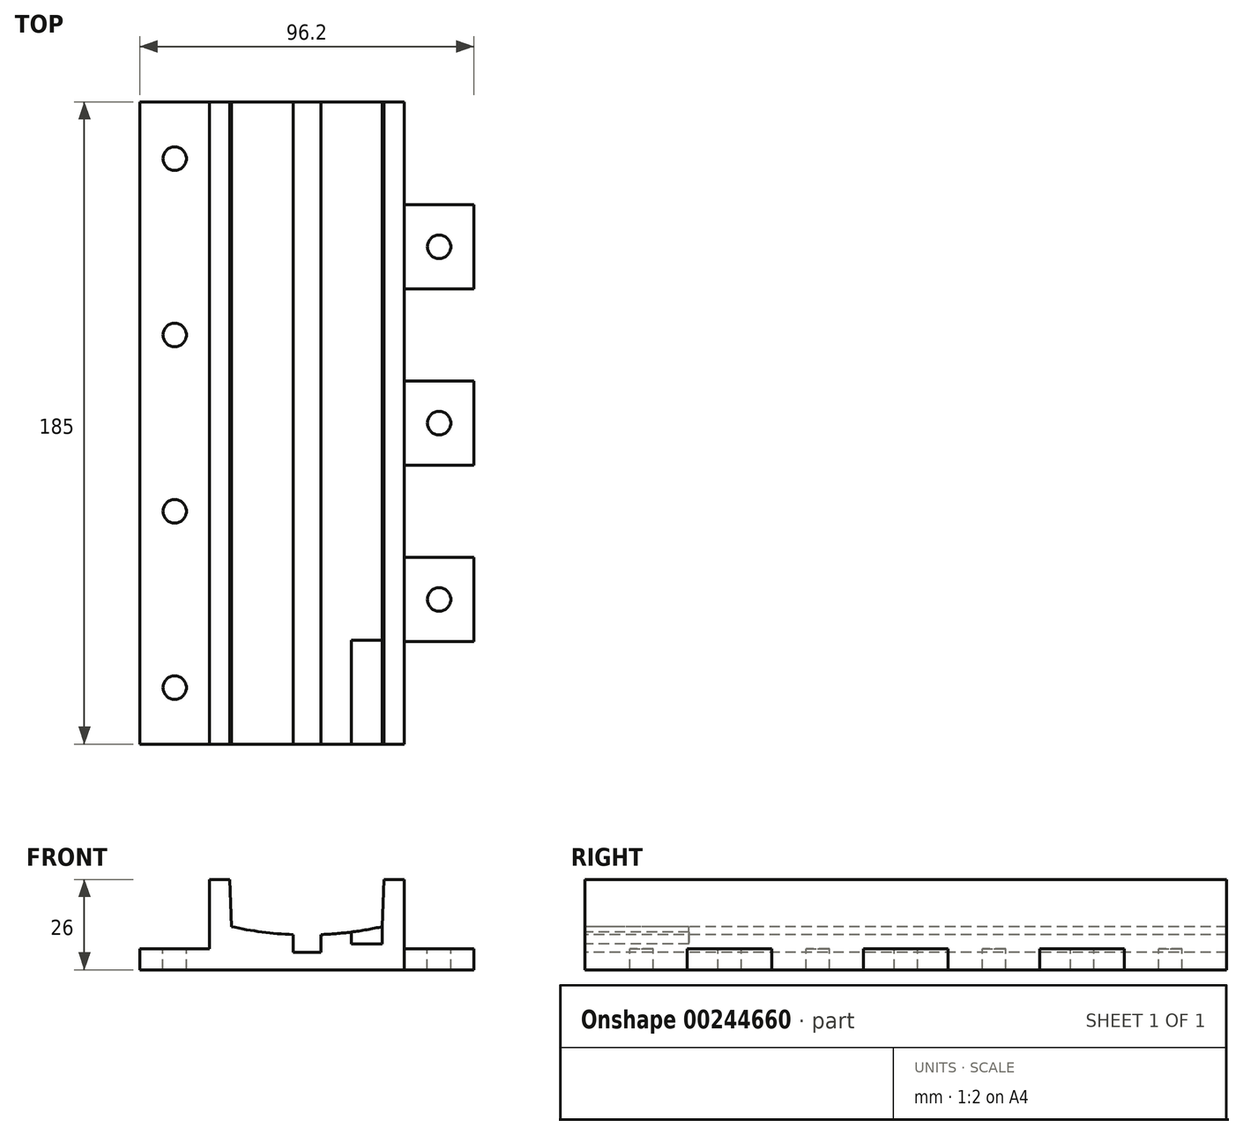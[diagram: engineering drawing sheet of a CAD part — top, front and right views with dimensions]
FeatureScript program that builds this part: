
annotation { "Feature Type Name" : "Feature", "Feature Type Description" : "" }
export const myFeature = defineFeature(function(context is Context, id is Id, definition is map)
    precondition{}
    {
        {
            var Q0;
            Q0=qCreatedBy(makeId("Front.planeOp"),FACE);
            var sketch = newSketch(context, id + "F0", { "sketchPlane" : qUnion([Q0])});
            skCircle(sketch, "E0", {"center": v(0, 0) * mm, "radius": 100.1 * mm});
            skLineSegment(sketch, "E1", {"start": v(0, 0) * mm, "end": v(0, -100.1) * mm});
            skLineSegment(sketch, "E2", {"start": v(0, -97.7) * mm, "end": v(21.77, -97.7) * mm});
            skLineSegment(sketch, "E3", {"start": v(0, -97.7) * mm, "end": v(-21.77, -97.7) * mm});
            skLineSegment(sketch, "E4", {"start": v(0, 0) * mm, "end": v(0, -27.77) * mm});
            skLineSegment(sketch, "E5", {"start": v(0, 0) * mm, "end": v(0, -84.15) * mm});
            skLineSegment(sketch, "E6", {"start": v(0, -84.15) * mm, "end": v(22.25, -84.15) * mm});
            skLineSegment(sketch, "E7", {"start": v(22.25, -84.15) * mm, "end": v(21.77, -97.7) * mm});
            skLineSegment(sketch, "E8", {"start": v(0, -84.15) * mm, "end": v(-22.25, -84.15) * mm});
            skLineSegment(sketch, "E9", {"start": v(-22.25, -84.15) * mm, "end": v(-21.77, -97.7) * mm});
            skLineSegment(sketch, "E10", {"start": v(-22.25, -84.15) * mm, "end": v(-28.1, -84.15) * mm});
            skLineSegment(sketch, "E11", {"start": v(-28.1, -84.15) * mm, "end": v(-28.1, -104.15) * mm});
            skLineSegment(sketch, "E12", {"start": v(-28.1, -104.15) * mm, "end": v(-48.1, -104.15) * mm});
            skLineSegment(sketch, "E13", {"start": v(-48.1, -104.15) * mm, "end": v(-48.1, -110.15) * mm});
            skLineSegment(sketch, "E14", {"start": v(-48.1, -110.15) * mm, "end": v(0, -110.15) * mm});
            skLineSegment(sketch, "E15", {"start": v(0, -110.15) * mm, "end": v(48.1, -110.15) * mm});
            skLineSegment(sketch, "E16", {"start": v(48.1, -110.15) * mm, "end": v(48.1, -104.15) * mm});
            skLineSegment(sketch, "E17", {"start": v(0, -97.7) * mm, "end": v(4, -97.7) * mm});
            skLineSegment(sketch, "E18", {"start": v(4, -105.15) * mm, "end": v(-4, -105.15) * mm});
            skLineSegment(sketch, "E19", {"start": v(-4, -105.15) * mm, "end": v(-4, -97.7) * mm});
            skLineSegment(sketch, "E20", {"start": v(4, -105.15) * mm, "end": v(4, -97.7) * mm});
            skLineSegment(sketch, "E21", {"start": v(21.77, -97.7) * mm, "end": v(12.77, -97.7) * mm});
            skLineSegment(sketch, "E22", {"start": v(12.77, -97.7) * mm, "end": v(12.77, -102.7) * mm});
            skLineSegment(sketch, "E23", {"start": v(12.77, -102.7) * mm, "end": v(21.77, -102.7) * mm});
            skLineSegment(sketch, "E24", {"start": v(21.77, -102.7) * mm, "end": v(21.77, -97.7) * mm});
            skLineSegment(sketch, "E25", {"start": v(22.25, -84.15) * mm, "end": v(28.1, -84.15) * mm});
            skLineSegment(sketch, "E26", {"start": v(28.1, -84.15) * mm, "end": v(28.1, -104.15) * mm});
            skLineSegment(sketch, "E27", {"start": v(28.1, -104.15) * mm, "end": v(48.1, -104.15) * mm});
            skSolve(sketch);
        }
        {
            var Q0;
            {var subQ0=sQuery(id+"F0.wireOp",EDGE,"E9");Q0=makeQuery(id+"F0.imprint","IMPRINT",FACE,{"disambiguationData":[TD([[makeQuery(id+"F0.imprint","IMPRINT",EDGE,{"derivedFrom":subQ0}),-1.0]])]});}
            var Q1;
            {var subQ4=sQuery(id+"F0.wireOp",EDGE,"E12");Q1=makeQuery(id+"F0.imprint","IMPRINT",FACE,{"disambiguationData":[TD([[makeQuery(id+"F0.imprint","IMPRINT",EDGE,{"derivedFrom":subQ4}),1.0]])]});}
            var Q2;
            {var subQ0=sQuery(id+"F0.wireOp",EDGE,"E7");Q2=makeQuery(id+"F0.imprint","IMPRINT",FACE,{"disambiguationData":[TD([[makeQuery(id+"F0.imprint","IMPRINT",EDGE,{"derivedFrom":subQ0}),1.0]])]});}
            var Q3;
            {var subQ0=sQuery(id+"F0.wireOp",EDGE,"E15");Q3=makeQuery(id+"F0.imprint","IMPRINT",FACE,{"disambiguationData":[TD([[makeQuery(id+"F0.imprint","IMPRINT",EDGE,{"derivedFrom":subQ0}),1.0]])]});}
            var Q4;
            {var subQ4=sQuery(id+"F0.wireOp",EDGE,"E23");Q4=makeQuery(id+"F0.imprint","IMPRINT",FACE,{"disambiguationData":[TD([[makeQuery(id+"F0.imprint","IMPRINT",EDGE,{"derivedFrom":subQ4}),1.0]])]});}
            extrude(context, id + "F1", {"entities" : qUnion([Q0, Q1, Q2, Q3, Q4]), "oppositeDirection" : true, "depth" : 185 * mm});
        }
        {
            var Q0;
            Q0=makeQuery(id+"F1.opExtrude","SWEPT_FACE",FACE,{"disambiguationData":[OSD([sQuery(id+"F0.wireOp",EDGE,"E12")])]});
            var sketch = newSketch(context, id + "F2", { "sketchPlane" : qUnion([Q0])});
            skLineSegment(sketch, "E28", {"start": v(-38.1, 0) * mm, "end": v(-38.1, 185) * mm});
            skLineSegment(sketch, "E29", {"start": v(-38.1, 0) * mm, "end": v(-38.1, 3.6) * mm});
            skLineSegment(sketch, "E30", {"start": v(-38.1, 3.6) * mm, "end": v(-38.1, 16.3) * mm});
            skLineSegment(sketch, "E31", {"start": v(-38.1, 16.3) * mm, "end": v(-38.1, 29) * mm});
            skLineSegment(sketch, "E32", {"start": v(-38.1, 29) * mm, "end": v(-38.1, 41.7) * mm});
            skLineSegment(sketch, "E33", {"start": v(-38.1, 41.7) * mm, "end": v(-38.1, 54.4) * mm});
            skLineSegment(sketch, "E34", {"start": v(-38.1, 54.4) * mm, "end": v(-38.1, 67.1) * mm});
            skLineSegment(sketch, "E35", {"start": v(-38.1, 67.1) * mm, "end": v(-38.1, 79.8) * mm});
            skLineSegment(sketch, "E36", {"start": v(-38.1, 79.8) * mm, "end": v(-38.1, 92.5) * mm});
            skLineSegment(sketch, "E37", {"start": v(-38.1, 92.5) * mm, "end": v(-38.1, 105.2) * mm});
            skLineSegment(sketch, "E38", {"start": v(-38.1, 105.2) * mm, "end": v(-38.1, 117.9) * mm});
            skLineSegment(sketch, "E39", {"start": v(-38.1, 117.9) * mm, "end": v(-38.1, 130.6) * mm});
            skLineSegment(sketch, "E40", {"start": v(-38.1, 130.6) * mm, "end": v(-38.1, 143.3) * mm});
            skLineSegment(sketch, "E41", {"start": v(-38.1, 143.3) * mm, "end": v(-38.1, 156) * mm});
            skLineSegment(sketch, "E42", {"start": v(-38.1, 156) * mm, "end": v(-38.1, 168.7) * mm});
            skLineSegment(sketch, "E43", {"start": v(-38.1, 168.7) * mm, "end": v(-38.1, 181.4) * mm});
            skLineSegment(sketch, "E44.bottom", {"start": v(-48.1, 3.6) * mm, "end": v(-28.1, 3.6) * mm});
            skLineSegment(sketch, "E44.top", {"start": v(-48.1, 29) * mm, "end": v(-28.1, 29) * mm});
            skLineSegment(sketch, "E44.left", {"start": v(-48.1, 3.6) * mm, "end": v(-48.1, 29) * mm});
            skLineSegment(sketch, "E44.right", {"start": v(-28.1, 3.6) * mm, "end": v(-28.1, 29) * mm});
            skPoint(sketch, "E44.middle", {"position": v(-38.1, 16.3) * mm});
            skLineSegment(sketch, "E45.bottom", {"start": v(-48.1, 54.4) * mm, "end": v(-28.1, 54.4) * mm});
            skLineSegment(sketch, "E45.top", {"start": v(-48.1, 79.8) * mm, "end": v(-28.1, 79.8) * mm});
            skLineSegment(sketch, "E45.left", {"start": v(-48.1, 54.4) * mm, "end": v(-48.1, 79.8) * mm});
            skLineSegment(sketch, "E45.right", {"start": v(-28.1, 54.4) * mm, "end": v(-28.1, 79.8) * mm});
            skPoint(sketch, "E45.middle", {"position": v(-38.1, 67.1) * mm});
            skLineSegment(sketch, "E46.bottom", {"start": v(-48.1, 105.2) * mm, "end": v(-28.1, 105.2) * mm});
            skLineSegment(sketch, "E46.top", {"start": v(-48.1, 130.6) * mm, "end": v(-28.1, 130.6) * mm});
            skLineSegment(sketch, "E46.left", {"start": v(-48.1, 105.2) * mm, "end": v(-48.1, 130.6) * mm});
            skLineSegment(sketch, "E46.right", {"start": v(-28.1, 105.2) * mm, "end": v(-28.1, 130.6) * mm});
            skPoint(sketch, "E46.middle", {"position": v(-38.1, 117.9) * mm});
            skLineSegment(sketch, "E47.bottom", {"start": v(-48.1, 156) * mm, "end": v(-28.1, 156) * mm});
            skLineSegment(sketch, "E47.top", {"start": v(-48.1, 181.4) * mm, "end": v(-28.1, 181.4) * mm});
            skLineSegment(sketch, "E47.left", {"start": v(-48.1, 156) * mm, "end": v(-48.1, 181.4) * mm});
            skLineSegment(sketch, "E47.right", {"start": v(-28.1, 156) * mm, "end": v(-28.1, 181.4) * mm});
            skPoint(sketch, "E47.middle", {"position": v(-38.1, 168.7) * mm});
            skLineSegment(sketch, "E48", {"start": v(-38.1, 41.7) * mm, "end": v(38.1, 41.7) * mm});
            skLineSegment(sketch, "E49", {"start": v(-38.1, 92.5) * mm, "end": v(38.1, 92.5) * mm});
            skLineSegment(sketch, "E50", {"start": v(-38.1, 143.3) * mm, "end": v(38.1, 143.3) * mm});
            skLineSegment(sketch, "E51.bottom", {"start": v(28.1, 29.55) * mm, "end": v(48.1, 29.55) * mm});
            skLineSegment(sketch, "E51.top", {"start": v(28.1, 53.85) * mm, "end": v(48.1, 53.85) * mm});
            skLineSegment(sketch, "E51.left", {"start": v(28.1, 29.55) * mm, "end": v(28.1, 53.85) * mm});
            skLineSegment(sketch, "E51.right", {"start": v(48.1, 29.55) * mm, "end": v(48.1, 53.85) * mm});
            skPoint(sketch, "E51.middle", {"position": v(38.1, 41.7) * mm});
            skLineSegment(sketch, "E52.bottom", {"start": v(28.1, 80.35) * mm, "end": v(48.1, 80.35) * mm});
            skLineSegment(sketch, "E52.top", {"start": v(28.1, 104.65) * mm, "end": v(48.1, 104.65) * mm});
            skLineSegment(sketch, "E52.left", {"start": v(28.1, 80.35) * mm, "end": v(28.1, 104.65) * mm});
            skLineSegment(sketch, "E52.right", {"start": v(48.1, 80.35) * mm, "end": v(48.1, 104.65) * mm});
            skPoint(sketch, "E52.middle", {"position": v(38.1, 92.5) * mm});
            skLineSegment(sketch, "E53.bottom", {"start": v(28.1, 131.15) * mm, "end": v(48.1, 131.15) * mm});
            skLineSegment(sketch, "E53.top", {"start": v(28.1, 155.45) * mm, "end": v(48.1, 155.45) * mm});
            skLineSegment(sketch, "E53.left", {"start": v(28.1, 131.15) * mm, "end": v(28.1, 155.45) * mm});
            skLineSegment(sketch, "E53.right", {"start": v(48.1, 131.15) * mm, "end": v(48.1, 155.45) * mm});
            skPoint(sketch, "E53.middle", {"position": v(38.1, 143.3) * mm});
            skLineSegment(sketch, "E54.top", {"start": v(28.1, -0.1) * mm, "end": v(48.1, -0.1) * mm});
            skLineSegment(sketch, "E54.left", {"start": v(28.1, 29.55) * mm, "end": v(28.1, -0.1) * mm});
            skLineSegment(sketch, "E54.right", {"start": v(48.1, 29.55) * mm, "end": v(48.1, -0.1) * mm});
            skLineSegment(sketch, "E55", {"start": v(28.1, 53.85) * mm, "end": v(28.1, 80.35) * mm});
            skLineSegment(sketch, "E56", {"start": v(48.1, 80.35) * mm, "end": v(48.1, 53.85) * mm});
            skLineSegment(sketch, "E57", {"start": v(48.1, 104.65) * mm, "end": v(48.1, 131.15) * mm});
            skLineSegment(sketch, "E58", {"start": v(28.1, 104.65) * mm, "end": v(28.1, 131.15) * mm});
            skLineSegment(sketch, "E59.top", {"start": v(28.1, 186.27) * mm, "end": v(48.1, 186.27) * mm});
            skLineSegment(sketch, "E59.left", {"start": v(28.1, 155.45) * mm, "end": v(28.1, 186.27) * mm});
            skLineSegment(sketch, "E59.right", {"start": v(48.1, 155.45) * mm, "end": v(48.1, 186.27) * mm});
            skSolve(sketch);
        }
        {
            var Q0;
            {var subQ4=sQuery(id+"F0.wireOp",EDGE,"E23");Q0=makeQuery(id+"F0.imprint","IMPRINT",FACE,{"disambiguationData":[TD([[makeQuery(id+"F0.imprint","IMPRINT",EDGE,{"derivedFrom":subQ4}),1.0]])]});}
            extrude(context, id + "F3", {"entities" : qUnion([Q0]), "operationType" : NewBodyOperationType.REMOVE, "oppositeDirection" : true, "depth" : 30 * mm});
        }
        {
            var Q0;
            {var subQ1=sQuery(id+"F2.wireOp",EDGE,"E32");Q0=makeQuery(id+"F2.imprint","IMPRINT",FACE,{"disambiguationData":[TD([[makeQuery(id+"F2.imprint","IMPRINT",EDGE,{"derivedFrom":subQ1}),1.0]])]});}
            var Q1;
            {var subQ5=sQuery(id+"F2.wireOp",EDGE,"E32");Q1=makeQuery(id+"F2.imprint","IMPRINT",FACE,{"disambiguationData":[TD([[makeQuery(id+"F2.imprint","IMPRINT",EDGE,{"derivedFrom":subQ5}),-1.0]])]});}
            var Q2;
            {var subQ5=sQuery(id+"F2.wireOp",EDGE,"E36");Q2=makeQuery(id+"F2.imprint","IMPRINT",FACE,{"disambiguationData":[TD([[makeQuery(id+"F2.imprint","IMPRINT",EDGE,{"derivedFrom":subQ5}),1.0]])]});}
            var Q3;
            {var subQ6=sQuery(id+"F2.wireOp",EDGE,"E36");Q3=makeQuery(id+"F2.imprint","IMPRINT",FACE,{"disambiguationData":[TD([[makeQuery(id+"F2.imprint","IMPRINT",EDGE,{"derivedFrom":subQ6}),-1.0]])]});}
            var Q4;
            {var subQ5=sQuery(id+"F2.wireOp",EDGE,"E40");Q4=makeQuery(id+"F2.imprint","IMPRINT",FACE,{"disambiguationData":[TD([[makeQuery(id+"F2.imprint","IMPRINT",EDGE,{"derivedFrom":subQ5}),1.0]])]});}
            var Q5;
            {var subQ1=sQuery(id+"F2.wireOp",EDGE,"E40");Q5=makeQuery(id+"F2.imprint","IMPRINT",FACE,{"disambiguationData":[TD([[makeQuery(id+"F2.imprint","IMPRINT",EDGE,{"derivedFrom":subQ1}),-1.0]])]});}
            var Q6;
            {var subQ3=sQuery(id+"F2.wireOp",EDGE,"Kx0XiVi7-Avo9-AEwS-amtW-mKGEHeSoishN.left");Q6=makeQuery(id+"F2.imprint","IMPRINT",FACE,{"disambiguationData":[TD([[makeQuery(id+"F2.imprint","IMPRINT",EDGE,{"derivedFrom":subQ3}),-1.0]])]});}
            var Q7;
            {var subQ3=sQuery(id+"F2.wireOp",EDGE,"Kx0XiVi7-Avo9-AEwS-amtW-mKGEHeSoishN.right");Q7=makeQuery(id+"F2.imprint","IMPRINT",FACE,{"disambiguationData":[TD([[makeQuery(id+"F2.imprint","IMPRINT",EDGE,{"derivedFrom":subQ3}),1.0]])]});}
            var Q8;
            {var subQ0=sQuery(id+"F2.wireOp",EDGE,"S2asEjbr-ItfW-8CEy-rvYZ-lPWanDjHSPZR");Q8=makeQuery(id+"F2.imprint","IMPRINT",FACE,{"disambiguationData":[TD([[makeQuery(id+"F2.imprint","IMPRINT",EDGE,{"derivedFrom":subQ0}),1.0]])]});}
            var Q9;
            {var subQ0=sQuery(id+"F2.wireOp",EDGE,"S2asEjbr-ItfW-8CEy-rvYZ-lPWanDjHSPZR");Q9=makeQuery(id+"F2.imprint","IMPRINT",FACE,{"disambiguationData":[TD([[makeQuery(id+"F2.imprint","IMPRINT",EDGE,{"derivedFrom":subQ0}),-1.0]])]});}
            var Q10;
            {var subQ0=sQuery(id+"F2.wireOp",EDGE,"JzAcrLFf-bXif-VgZO-E9dv-qHN1DuVPC9Om");Q10=makeQuery(id+"F2.imprint","IMPRINT",FACE,{"disambiguationData":[TD([[makeQuery(id+"F2.imprint","IMPRINT",EDGE,{"derivedFrom":subQ0}),1.0]])]});}
            var Q11;
            {var subQ0=sQuery(id+"F2.wireOp",EDGE,"JzAcrLFf-bXif-VgZO-E9dv-qHN1DuVPC9Om");Q11=makeQuery(id+"F2.imprint","IMPRINT",FACE,{"disambiguationData":[TD([[makeQuery(id+"F2.imprint","IMPRINT",EDGE,{"derivedFrom":subQ0}),-1.0]])]});}
            var Q12;
            {var subQ0=sQuery(id+"F2.wireOp",EDGE,"GFUPfIHZ-XsYj-PfAZ-TFsL-zxp98WBQijr5");Q12=makeQuery(id+"F2.imprint","IMPRINT",FACE,{"disambiguationData":[TD([[makeQuery(id+"F2.imprint","IMPRINT",EDGE,{"derivedFrom":subQ0}),1.0]])]});}
            var Q13;
            {var subQ0=sQuery(id+"F2.wireOp",EDGE,"GFUPfIHZ-XsYj-PfAZ-TFsL-zxp98WBQijr5");Q13=makeQuery(id+"F2.imprint","IMPRINT",FACE,{"disambiguationData":[TD([[makeQuery(id+"F2.imprint","IMPRINT",EDGE,{"derivedFrom":subQ0}),-1.0]])]});}
            var Q14;
            {var subQ0=sQuery(id+"F2.wireOp",EDGE,"P7enYfgo-VQvh-D6Px-TYbV-wwwR8uyFIA23");Q14=makeQuery(id+"F2.imprint","IMPRINT",FACE,{"disambiguationData":[TD([[makeQuery(id+"F2.imprint","IMPRINT",EDGE,{"derivedFrom":subQ0}),-1.0]])]});}
            var Q15;
            {var subQ0=sQuery(id+"F2.wireOp",EDGE,"P7enYfgo-VQvh-D6Px-TYbV-wwwR8uyFIA23");Q15=makeQuery(id+"F2.imprint","IMPRINT",FACE,{"disambiguationData":[TD([[makeQuery(id+"F2.imprint","IMPRINT",EDGE,{"derivedFrom":subQ0}),1.0]])]});}
            var Q16;
            {var subQ0=sQuery(id+"F2.wireOp",EDGE,"j36Web8z-IaPA-VSiz-Xd4a-VODAtwFXN5Jg");Q16=makeQuery(id+"F2.imprint","IMPRINT",FACE,{"disambiguationData":[TD([[makeQuery(id+"F2.imprint","IMPRINT",EDGE,{"derivedFrom":subQ0}),-1.0]])]});}
            var Q17;
            {var subQ0=sQuery(id+"F2.wireOp",EDGE,"j36Web8z-IaPA-VSiz-Xd4a-VODAtwFXN5Jg");Q17=makeQuery(id+"F2.imprint","IMPRINT",FACE,{"disambiguationData":[TD([[makeQuery(id+"F2.imprint","IMPRINT",EDGE,{"derivedFrom":subQ0}),1.0]])]});}
            var Q18;
            {var subQ0=sQuery(id+"F2.wireOp",EDGE,"E33");Q18=makeQuery(id+"F2.imprint","IMPRINT",FACE,{"disambiguationData":[TD([[makeQuery(id+"F2.imprint","IMPRINT",EDGE,{"derivedFrom":subQ0}),-1.0]])]});}
            var Q19;
            {var subQ0=sQuery(id+"F2.wireOp",EDGE,"E37");Q19=makeQuery(id+"F2.imprint","IMPRINT",FACE,{"disambiguationData":[TD([[makeQuery(id+"F2.imprint","IMPRINT",EDGE,{"derivedFrom":subQ0}),-1.0]])]});}
            var Q20;
            {var subQ0=sQuery(id+"F2.wireOp",EDGE,"E41");Q20=makeQuery(id+"F2.imprint","IMPRINT",FACE,{"disambiguationData":[TD([[makeQuery(id+"F2.imprint","IMPRINT",EDGE,{"derivedFrom":subQ0}),-1.0]])]});}
            var Q21;
            Q21=makeQuery(id+"F2.imprint","IMPRINT",FACE,{"disambiguationData":[TD([[makeQuery(id+"F2.imprint","IMPRINT",EDGE,{"derivedFrom":sQuery(id+"F2.wireOp",EDGE,"E51.bottom")}),-1.0]])]});
            var Q22;
            Q22=makeQuery(id+"F2.imprint","IMPRINT",FACE,{"disambiguationData":[TD([[makeQuery(id+"F2.imprint","IMPRINT",EDGE,{"derivedFrom":sQuery(id+"F2.wireOp",EDGE,"E51.top")}),1.0]])]});
            var Q23;
            Q23=makeQuery(id+"F2.imprint","IMPRINT",FACE,{"disambiguationData":[TD([[makeQuery(id+"F2.imprint","IMPRINT",EDGE,{"derivedFrom":sQuery(id+"F2.wireOp",EDGE,"E52.top")}),1.0]])]});
            var Q24;
            Q24=makeQuery(id+"F2.imprint","IMPRINT",FACE,{"disambiguationData":[TD([[makeQuery(id+"F2.imprint","IMPRINT",EDGE,{"derivedFrom":sQuery(id+"F2.wireOp",EDGE,"E53.top")}),1.0]])]});
            extrude(context, id + "F4", {"entities" : qUnion([Q0, Q1, Q2, Q3, Q4, Q5, Q6, Q7, Q8, Q9, Q10, Q11, Q12, Q13, Q14, Q15, Q16, Q17, Q18, Q19, Q20, Q21, Q22, Q23, Q24]), "operationType" : NewBodyOperationType.REMOVE, "oppositeDirection" : true, "depth" : 25 * mm});
        }
        {
            var Q0;
            Q0=sQuery(id+"F2.wireOp",VERTEX,"E45.middle");
            var Q1;
            Q1=sQuery(id+"F2.wireOp",VERTEX,"E44.middle");
            var Q2;
            Q2=sQuery(id+"F2.wireOp",VERTEX,"E46.middle");
            var Q3;
            Q3=sQuery(id+"F2.wireOp",VERTEX,"E47.middle");
            var Q4;
            Q4=sQuery(id+"F2.wireOp",VERTEX,"62n5RLEP-ac1f-hWt1-C9TF-4L55woSEdjSa.end");
            var Q5;
            Q5=sQuery(id+"F2.wireOp",VERTEX,"MW1VYb7V-1YSa-GrZu-T1Yo-UyaLmu48d9Nu.end");
            var Q6;
            Q6=sQuery(id+"F2.wireOp",VERTEX,"2mOHiBT3-vwvd-zI96-IaNh-d59bQ1CSOoLX.end");
            var Q7;
            Q7=sQuery(id+"F2.wireOp",VERTEX,"E52.middle");
            var Q8;
            Q8=sQuery(id+"F2.wireOp",VERTEX,"E53.middle");
            var Q9;
            Q9=sQuery(id+"F2.wireOp",VERTEX,"E51.middle");
            var Q10;
            Q10=makeQuery(id+"F1.opExtrude","SWEPT_BODY",BODY,{"disambiguationData":[OSD([sQuery(id+"F0.wireOp",EDGE,"E0"),sQuery(id+"F0.wireOp",EDGE,"E7"),sQuery(id+"F0.wireOp",EDGE,"E9"),sQuery(id+"F0.wireOp",EDGE,"E10"),sQuery(id+"F0.wireOp",EDGE,"E11"),sQuery(id+"F0.wireOp",EDGE,"E12"),sQuery(id+"F0.wireOp",EDGE,"E13"),sQuery(id+"F0.wireOp",EDGE,"E14"),sQuery(id+"F0.wireOp",EDGE,"E15"),sQuery(id+"F0.wireOp",EDGE,"E16"),sQuery(id+"F0.wireOp",EDGE,"RZF5u4SO-StZo-GAtQ-oNK3-tfnz65FCON6z"),sQuery(id+"F0.wireOp",EDGE,"KuSa3ER0-xW1w-B797-YUfY-ffhBq145HGXg"),sQuery(id+"F0.wireOp",EDGE,"72fn3s0H-gvsu-v3U4-Vofv-ftGWhK2hwAUf"),sQuery(id+"F0.wireOp",EDGE,"E18"),sQuery(id+"F0.wireOp",EDGE,"E19"),sQuery(id+"F0.wireOp",EDGE,"E20")])]});
            hole(context, id + "F5", {"style" : HoleStyle.SIMPLE, "endStyle" : HoleEndStyle.THROUGH, "standardTappedOrClearance" : lookupTablePath({ "standard" : "ANSI", "fit" : "Normal (ASME)", "size" : "1/4", "type" : "Clearance" }), "standardBlindInLast" : lookupTablePath({ "fit" : "Free", "standard" : "ANSI", "size" : "1/4", "type" : "Clearance" }), "holeDiameter" : 6.76 * mm, "tappedDepth" : 12 * mm, "tapClearance" : 3, "locations" : qUnion([Q0, Q1, Q2, Q3, Q4, Q5, Q6, Q7, Q8, Q9]), "scope" : qUnion([Q10])});
        }
    });
